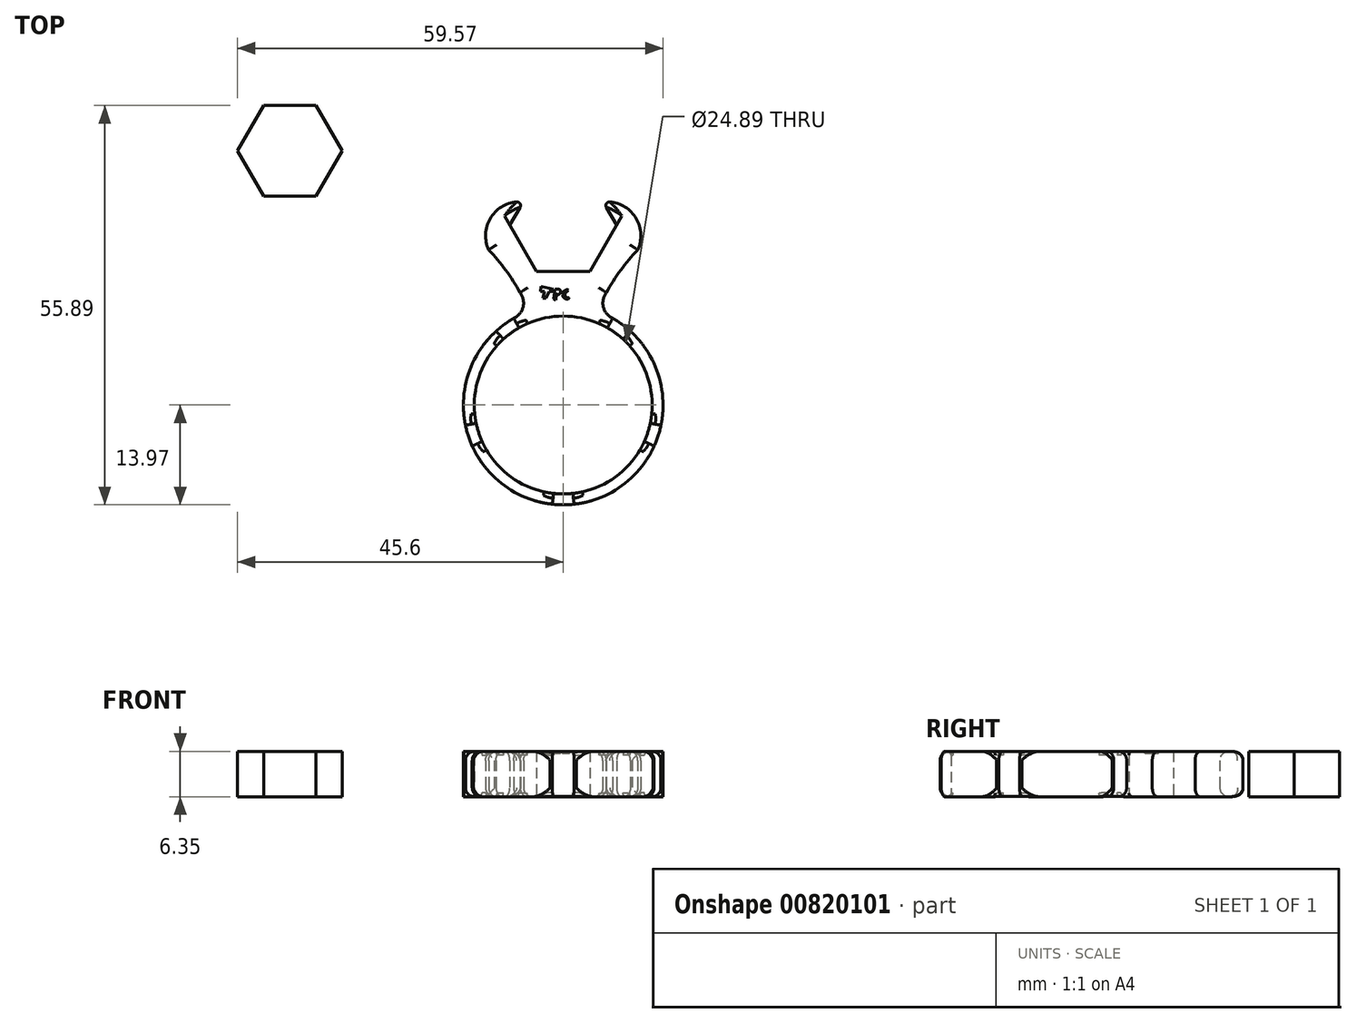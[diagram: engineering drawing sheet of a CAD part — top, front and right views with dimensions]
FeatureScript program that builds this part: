
annotation { "Feature Type Name" : "Feature", "Feature Type Description" : "" }
export const myFeature = defineFeature(function(context is Context, id is Id, definition is map)
    precondition{}
    {
        {
            var Q0;
            Q0=qCreatedBy(makeId("Top.planeOp"),FACE);
            var sketch = newSketch(context, id + "F0", { "sketchPlane" : qUnion([Q0])});
            skCircle(sketch, "E0", {"center": v(0, 0) * mm, "radius": 31.75 * mm, "construction": true});
            skCircle(sketch, "E1", {"center": v(0, 0) * mm, "radius": 12.45 * mm});
            skCircle(sketch, "E2.cCircle", {"center": v(0, 25.18) * mm, "radius": 6.48 * mm, "construction": true});
            skLineSegment(sketch, "E2.0", {"start": v(-3.74, 18.7) * mm, "end": v(-7.48, 25.18) * mm});
            skLineSegment(sketch, "E2.1", {"start": v(-7.48, 25.18) * mm, "end": v(-3.74, 31.66) * mm});
            skLineSegment(sketch, "E2.2", {"start": v(-3.74, 31.66) * mm, "end": v(3.74, 31.66) * mm});
            skLineSegment(sketch, "E2.3", {"start": v(3.74, 31.66) * mm, "end": v(7.48, 25.18) * mm});
            skLineSegment(sketch, "E2.4", {"start": v(7.48, 25.18) * mm, "end": v(3.74, 18.7) * mm});
            skLineSegment(sketch, "E2.5", {"start": v(3.74, 18.7) * mm, "end": v(-3.74, 18.7) * mm});
            skPoint(sketch, "E2.0.midPoint", {"position": v(-5.5, 18.96) * mm});
            skCircle(sketch, "E3", {"center": v(0, 0) * mm, "radius": 13.97 * mm});
            skArc(sketch, "E4", {"start": v(-5.6, 28.42) * mm, "mid": v(-9.97, 26.47) * mm, "end": v(-10.43, 21.7) * mm});
            skArc(sketch, "E5", {"start": v(-6.03, 15.72) * mm, "mid": v(-8.04, 18.85) * mm, "end": v(-10.43, 21.7) * mm});
            skArc(sketch, "E6", {"start": v(-6.92, 12.14) * mm, "mid": v(-5.62, 13.72) * mm, "end": v(-6.03, 15.72) * mm});
            skArc(sketch, "E7.MirrorCS", {"start": v(5.6, 28.42) * mm, "mid": v(9.97, 26.47) * mm, "end": v(10.43, 21.7) * mm});
            skArc(sketch, "E8.MirrorCS", {"start": v(6.03, 15.72) * mm, "mid": v(8.04, 18.85) * mm, "end": v(10.43, 21.7) * mm});
            skArc(sketch, "E9.MirrorCS", {"start": v(6.92, 12.14) * mm, "mid": v(5.62, 13.72) * mm, "end": v(6.03, 15.72) * mm});
            skArc(sketch, "E10.1.0", {"start": v(-25.3, 14.12) * mm, "mid": v(-22.09, 17.66) * mm, "end": v(-17.42, 16.63) * mm});
            skArc(sketch, "E10.1.1", {"start": v(-13.1, 10.6) * mm, "mid": v(-15.45, 13.47) * mm, "end": v(-17.42, 16.63) * mm});
            skCircle(sketch, "E10.1.2", {"center": v(-23.95, 7.78) * mm, "radius": 6.48 * mm, "construction": true});
            skLineSegment(sketch, "E10.1.3", {"start": v(-31.26, 6.23) * mm, "end": v(-28.95, 13.34) * mm});
            skLineSegment(sketch, "E10.1.4", {"start": v(-21.64, 14.9) * mm, "end": v(-16.63, 9.34) * mm});
            skArc(sketch, "E10.1.5", {"start": v(-28.76, 3.45) * mm, "mid": v(-28.25, -1.3) * mm, "end": v(-23.87, -3.21) * mm});
            skArc(sketch, "E10.1.6", {"start": v(-16.82, -0.87) * mm, "mid": v(-20.42, -1.82) * mm, "end": v(-23.87, -3.21) * mm});
            skPoint(sketch, "E10.1.7", {"position": v(-19.73, 0.63) * mm});
            skArc(sketch, "E10.1.8", {"start": v(-9.4, 10.33) * mm, "mid": v(-11.31, 9.58) * mm, "end": v(-13.1, 10.6) * mm});
            skLineSegment(sketch, "E10.1.9", {"start": v(-18.94, 2.22) * mm, "end": v(-26.26, 0.67) * mm});
            skLineSegment(sketch, "E10.1.10", {"start": v(-26.26, 0.67) * mm, "end": v(-31.26, 6.23) * mm});
            skLineSegment(sketch, "E10.1.11", {"start": v(-16.63, 9.34) * mm, "end": v(-18.94, 2.22) * mm});
            skArc(sketch, "E10.1.12", {"start": v(-13.68, -2.83) * mm, "mid": v(-14.78, -1.1) * mm, "end": v(-16.82, -0.87) * mm});
            skLineSegment(sketch, "E10.1.13", {"start": v(-28.95, 13.34) * mm, "end": v(-21.64, 14.9) * mm});
            skArc(sketch, "E10.2.0", {"start": v(-21.24, -19.7) * mm, "mid": v(-23.63, -15.55) * mm, "end": v(-21.2, -11.43) * mm});
            skArc(sketch, "E10.2.1", {"start": v(-14.12, -9.18) * mm, "mid": v(-17.59, -10.53) * mm, "end": v(-21.2, -11.43) * mm});
            skCircle(sketch, "E10.2.2", {"center": v(-14.8, -20.37) * mm, "radius": 6.48 * mm, "construction": true});
            skLineSegment(sketch, "E10.2.3", {"start": v(-15.58, -27.8) * mm, "end": v(-21.63, -23.41) * mm});
            skLineSegment(sketch, "E10.2.4", {"start": v(-20.85, -15.97) * mm, "end": v(-14.02, -12.93) * mm});
            skArc(sketch, "E10.2.5", {"start": v(-12.17, -26.29) * mm, "mid": v(-7.49, -27.27) * mm, "end": v(-4.32, -23.7) * mm});
            skArc(sketch, "E10.2.6", {"start": v(-4.37, -16.26) * mm, "mid": v(-4.58, -19.98) * mm, "end": v(-4.32, -23.7) * mm});
            skPoint(sketch, "E10.2.7", {"position": v(-6.7, -18.57) * mm});
            skArc(sketch, "E10.2.8", {"start": v(-12.73, -5.75) * mm, "mid": v(-12.6, -7.8) * mm, "end": v(-14.12, -9.18) * mm});
            skLineSegment(sketch, "E10.2.9", {"start": v(-7.97, -17.33) * mm, "end": v(-8.75, -24.77) * mm});
            skLineSegment(sketch, "E10.2.10", {"start": v(-8.75, -24.77) * mm, "end": v(-15.58, -27.8) * mm});
            skLineSegment(sketch, "E10.2.11", {"start": v(-14.02, -12.93) * mm, "end": v(-7.97, -17.33) * mm});
            skArc(sketch, "E10.2.12", {"start": v(-1.54, -13.89) * mm, "mid": v(-3.52, -14.4) * mm, "end": v(-4.37, -16.26) * mm});
            skLineSegment(sketch, "E10.2.13", {"start": v(-21.63, -23.41) * mm, "end": v(-20.85, -15.97) * mm});
            skArc(sketch, "E10.3.0", {"start": v(12.17, -26.29) * mm, "mid": v(7.49, -27.27) * mm, "end": v(4.32, -23.7) * mm});
            skArc(sketch, "E10.3.1", {"start": v(4.37, -16.26) * mm, "mid": v(4.58, -19.98) * mm, "end": v(4.32, -23.7) * mm});
            skCircle(sketch, "E10.3.2", {"center": v(14.8, -20.37) * mm, "radius": 6.48 * mm, "construction": true});
            skLineSegment(sketch, "E10.3.3", {"start": v(21.63, -23.41) * mm, "end": v(15.58, -27.8) * mm});
            skLineSegment(sketch, "E10.3.4", {"start": v(8.75, -24.77) * mm, "end": v(7.97, -17.33) * mm});
            skArc(sketch, "E10.3.5", {"start": v(21.24, -19.7) * mm, "mid": v(23.63, -15.55) * mm, "end": v(21.2, -11.43) * mm});
            skArc(sketch, "E10.3.6", {"start": v(14.12, -9.18) * mm, "mid": v(17.59, -10.53) * mm, "end": v(21.2, -11.43) * mm});
            skPoint(sketch, "E10.3.7", {"position": v(15.6, -12.1) * mm});
            skArc(sketch, "E10.3.8", {"start": v(1.54, -13.89) * mm, "mid": v(3.52, -14.4) * mm, "end": v(4.37, -16.26) * mm});
            skLineSegment(sketch, "E10.3.9", {"start": v(14.02, -12.93) * mm, "end": v(20.85, -15.97) * mm});
            skLineSegment(sketch, "E10.3.10", {"start": v(20.85, -15.97) * mm, "end": v(21.63, -23.41) * mm});
            skLineSegment(sketch, "E10.3.11", {"start": v(7.97, -17.33) * mm, "end": v(14.02, -12.93) * mm});
            skArc(sketch, "E10.3.12", {"start": v(12.73, -5.75) * mm, "mid": v(12.6, -7.8) * mm, "end": v(14.12, -9.18) * mm});
            skLineSegment(sketch, "E10.3.13", {"start": v(15.58, -27.8) * mm, "end": v(8.75, -24.77) * mm});
            skArc(sketch, "E10.4.0", {"start": v(28.76, 3.45) * mm, "mid": v(28.25, -1.3) * mm, "end": v(23.87, -3.21) * mm});
            skArc(sketch, "E10.4.1", {"start": v(16.82, -0.87) * mm, "mid": v(20.42, -1.82) * mm, "end": v(23.87, -3.21) * mm});
            skCircle(sketch, "E10.4.2", {"center": v(23.95, 7.78) * mm, "radius": 6.48 * mm, "construction": true});
            skLineSegment(sketch, "E10.4.3", {"start": v(28.95, 13.34) * mm, "end": v(31.26, 6.23) * mm});
            skLineSegment(sketch, "E10.4.4", {"start": v(26.26, 0.67) * mm, "end": v(18.94, 2.22) * mm});
            skArc(sketch, "E10.4.5", {"start": v(25.3, 14.12) * mm, "mid": v(22.09, 17.66) * mm, "end": v(17.42, 16.63) * mm});
            skArc(sketch, "E10.4.6", {"start": v(13.1, 10.6) * mm, "mid": v(15.45, 13.47) * mm, "end": v(17.42, 16.63) * mm});
            skPoint(sketch, "E10.4.7", {"position": v(16.33, 11.09) * mm});
            skArc(sketch, "E10.4.8", {"start": v(13.68, -2.83) * mm, "mid": v(14.78, -1.1) * mm, "end": v(16.82, -0.87) * mm});
            skLineSegment(sketch, "E10.4.9", {"start": v(16.63, 9.34) * mm, "end": v(21.64, 14.9) * mm});
            skLineSegment(sketch, "E10.4.10", {"start": v(21.64, 14.9) * mm, "end": v(28.95, 13.34) * mm});
            skLineSegment(sketch, "E10.4.11", {"start": v(18.94, 2.22) * mm, "end": v(16.63, 9.34) * mm});
            skArc(sketch, "E10.4.12", {"start": v(9.4, 10.33) * mm, "mid": v(11.31, 9.58) * mm, "end": v(13.1, 10.6) * mm});
            skLineSegment(sketch, "E10.4.13", {"start": v(31.26, 6.23) * mm, "end": v(26.26, 0.67) * mm});
            skSolve(sketch);
        }
        {
            var Q0;
            {var subQ0=sQuery(id+"F0.wireOp",EDGE,"08dda1b8-4bbb-4ccd-a0d6-4031cab699ba.4.4.0");var subQ1=sQuery(id+"F0.wireOp",EDGE,"E1");var subQ2=makeQuery(id+"F0.imprint","INTERSECT",VERTEX,{"derivedFrom":[subQ1,subQ0]});Q0=makeQuery(id+"F0.imprint","IMPRINT",FACE,{"disambiguationData":[TD([[makeQuery(id+"F0.imprint","IMPRINT",EDGE,{"disambiguationData":[TD([[subQ2,-1.0]])],"derivedFrom":subQ1}),-1.0]])]});}
            var Q1;
            {var subQ0=sQuery(id+"F0.wireOp",EDGE,"08dda1b8-4bbb-4ccd-a0d6-4031cab699ba.17.3.0");var subQ1=sQuery(id+"F0.wireOp",EDGE,"E1");var subQ2=makeQuery(id+"F0.imprint","INTERSECT",VERTEX,{"derivedFrom":[subQ1,subQ0]});Q1=makeQuery(id+"F0.imprint","IMPRINT",FACE,{"disambiguationData":[TD([[makeQuery(id+"F0.imprint","IMPRINT",EDGE,{"disambiguationData":[TD([[subQ2,-1.0]])],"derivedFrom":subQ1}),-1.0]])]});}
            var Q2;
            {var subQ0=sQuery(id+"F0.wireOp",EDGE,"08dda1b8-4bbb-4ccd-a0d6-4031cab699ba.4.3.0");var subQ1=sQuery(id+"F0.wireOp",EDGE,"E1");var subQ2=makeQuery(id+"F0.imprint","INTERSECT",VERTEX,{"derivedFrom":[subQ1,subQ0]});Q2=makeQuery(id+"F0.imprint","IMPRINT",FACE,{"disambiguationData":[TD([[makeQuery(id+"F0.imprint","IMPRINT",EDGE,{"disambiguationData":[TD([[subQ2,-1.0]])],"derivedFrom":subQ1}),-1.0]])]});}
            var Q3;
            {var subQ0=sQuery(id+"F0.wireOp",EDGE,"133b7ee5-6936-4400-ab5c-c1a8c481468b.2.5");var subQ1=sQuery(id+"F0.wireOp",EDGE,"E1");var subQ2=makeQuery(id+"F0.imprint","INTERSECT",VERTEX,{"derivedFrom":[subQ1,subQ0]});Q3=makeQuery(id+"F0.imprint","IMPRINT",FACE,{"disambiguationData":[TD([[makeQuery(id+"F0.imprint","IMPRINT",EDGE,{"disambiguationData":[TD([[subQ2,-1.0]])],"derivedFrom":subQ1}),-1.0]])]});}
            var Q4;
            {var subQ0=sQuery(id+"F0.wireOp",EDGE,"133b7ee5-6936-4400-ab5c-c1a8c481468b.2.1");var subQ1=sQuery(id+"F0.wireOp",EDGE,"E1");var subQ2=makeQuery(id+"F0.imprint","INTERSECT",VERTEX,{"derivedFrom":[subQ1,subQ0]});Q4=makeQuery(id+"F0.imprint","IMPRINT",FACE,{"disambiguationData":[TD([[makeQuery(id+"F0.imprint","IMPRINT",EDGE,{"disambiguationData":[TD([[subQ2,-1.0]])],"derivedFrom":subQ1}),-1.0]])]});}
            var Q5;
            {var subQ0=sQuery(id+"F0.wireOp",EDGE,"133b7ee5-6936-4400-ab5c-c1a8c481468b.1.5");var subQ1=sQuery(id+"F0.wireOp",EDGE,"E1");var subQ2=makeQuery(id+"F0.imprint","INTERSECT",VERTEX,{"derivedFrom":[subQ1,subQ0]});Q5=makeQuery(id+"F0.imprint","IMPRINT",FACE,{"disambiguationData":[TD([[makeQuery(id+"F0.imprint","IMPRINT",EDGE,{"disambiguationData":[TD([[subQ2,-1.0]])],"derivedFrom":subQ1}),-1.0]])]});}
            var Q6;
            {var subQ0=sQuery(id+"F0.wireOp",EDGE,"133b7ee5-6936-4400-ab5c-c1a8c481468b.1.1");var subQ1=sQuery(id+"F0.wireOp",EDGE,"E1");var subQ2=makeQuery(id+"F0.imprint","INTERSECT",VERTEX,{"derivedFrom":[subQ1,subQ0]});Q6=makeQuery(id+"F0.imprint","IMPRINT",FACE,{"disambiguationData":[TD([[makeQuery(id+"F0.imprint","IMPRINT",EDGE,{"disambiguationData":[TD([[subQ2,-1.0]])],"derivedFrom":subQ1}),-1.0]])]});}
            var Q7;
            {var subQ0=sQuery(id+"F0.wireOp",EDGE,"d495b0eb-ba1d-4a21-93e3-987e0228af5a");var subQ1=sQuery(id+"F0.wireOp",EDGE,"E1");var subQ2=makeQuery(id+"F0.imprint","INTERSECT",VERTEX,{"derivedFrom":[subQ1,subQ0]});Q7=makeQuery(id+"F0.imprint","IMPRINT",FACE,{"disambiguationData":[TD([[makeQuery(id+"F0.imprint","IMPRINT",EDGE,{"disambiguationData":[TD([[subQ2,-1.0]])],"derivedFrom":subQ1}),-1.0]])]});}
            var Q8;
            {var subQ0=sQuery(id+"F0.wireOp",EDGE,"d495b0eb-ba1d-4a21-93e3-987e0228af5a");var subQ1=sQuery(id+"F0.wireOp",EDGE,"E1");var subQ2=makeQuery(id+"F0.imprint","INTERSECT",VERTEX,{"derivedFrom":[subQ1,subQ0]});Q8=makeQuery(id+"F0.imprint","IMPRINT",FACE,{"disambiguationData":[TD([[makeQuery(id+"F0.imprint","IMPRINT",EDGE,{"disambiguationData":[TD([[subQ2,1.0]])],"derivedFrom":subQ1}),-1.0]])]});}
            var Q9;
            {var subQ0=sQuery(id+"F0.wireOp",EDGE,"9611d97b-251f-4bb5-bbc4-e98456876ea10.MirrorCS");var subQ1=sQuery(id+"F0.wireOp",EDGE,"E1");var subQ2=makeQuery(id+"F0.imprint","INTERSECT",VERTEX,{"derivedFrom":[subQ1,subQ0]});Q9=makeQuery(id+"F0.imprint","IMPRINT",FACE,{"disambiguationData":[TD([[makeQuery(id+"F0.imprint","IMPRINT",EDGE,{"disambiguationData":[TD([[subQ2,1.0]])],"derivedFrom":subQ1}),-1.0]])]});}
            var Q10;
            {var subQ2=sQuery(id+"F0.wireOp",EDGE,"E2.0");Q10=makeQuery(id+"F0.imprint","IMPRINT",FACE,{"disambiguationData":[TD([[makeQuery(id+"F0.imprint","IMPRINT",EDGE,{"derivedFrom":subQ2}),1.0]])]});}
            var Q11;
            Q11=makeQuery(id+"F0.imprint","IMPRINT",FACE,{"disambiguationData":[TD([[makeQuery(id+"F0.imprint","IMPRINT",EDGE,{"derivedFrom":sQuery(id+"F0.wireOp",EDGE,"08dda1b8-4bbb-4ccd-a0d6-4031cab699ba.11.4.0")}),1.0]])]});
            var Q12;
            Q12=makeQuery(id+"F0.imprint","IMPRINT",FACE,{"disambiguationData":[TD([[makeQuery(id+"F0.imprint","IMPRINT",EDGE,{"derivedFrom":sQuery(id+"F0.wireOp",EDGE,"08dda1b8-4bbb-4ccd-a0d6-4031cab699ba.11.3.0")}),1.0]])]});
            var Q13;
            {var subQ1=sQuery(id+"F0.wireOp",EDGE,"133b7ee5-6936-4400-ab5c-c1a8c481468b.2.0");Q13=makeQuery(id+"F0.imprint","IMPRINT",FACE,{"disambiguationData":[TD([[makeQuery(id+"F0.imprint","IMPRINT",EDGE,{"derivedFrom":subQ1}),1.0]])]});}
            var Q14;
            {var subQ1=sQuery(id+"F0.wireOp",EDGE,"133b7ee5-6936-4400-ab5c-c1a8c481468b.1.0");Q14=makeQuery(id+"F0.imprint","IMPRINT",FACE,{"disambiguationData":[TD([[makeQuery(id+"F0.imprint","IMPRINT",EDGE,{"derivedFrom":subQ1}),1.0]])]});}
            var Q15;
            {var subQ8=sQuery(id+"F0.wireOp",EDGE,"E10.1.0");Q15=makeQuery(id+"F0.imprint","IMPRINT",FACE,{"disambiguationData":[TD([[makeQuery(id+"F0.imprint","IMPRINT",EDGE,{"derivedFrom":subQ8}),-1.0]])]});}
            var Q16;
            {var subQ10=sQuery(id+"F0.wireOp",EDGE,"E10.2.0");Q16=makeQuery(id+"F0.imprint","IMPRINT",FACE,{"disambiguationData":[TD([[makeQuery(id+"F0.imprint","IMPRINT",EDGE,{"derivedFrom":subQ10}),-1.0]])]});}
            var Q17;
            {var subQ10=sQuery(id+"F0.wireOp",EDGE,"E10.3.0");Q17=makeQuery(id+"F0.imprint","IMPRINT",FACE,{"disambiguationData":[TD([[makeQuery(id+"F0.imprint","IMPRINT",EDGE,{"derivedFrom":subQ10}),-1.0]])]});}
            var Q18;
            {var subQ11=sQuery(id+"F0.wireOp",EDGE,"E10.4.0");Q18=makeQuery(id+"F0.imprint","IMPRINT",FACE,{"disambiguationData":[TD([[makeQuery(id+"F0.imprint","IMPRINT",EDGE,{"derivedFrom":subQ11}),-1.0]])]});}
            extrude(context, id + "F1", {"entities" : qUnion([Q0, Q1, Q2, Q3, Q4, Q5, Q6, Q7, Q8, Q9, Q10, Q11, Q12, Q13, Q14, Q15, Q16, Q17, Q18]), "depth" : 6.35 * mm, "offsetDistance" : 25.4 * mm});
        }
        {
            var Q0;
            Q0=qCreatedBy(makeId("Top.planeOp"),FACE);
            var sketch = newSketch(context, id + "F2", { "sketchPlane" : qUnion([Q0])});
            skCircle(sketch, "E11.cCircle", {"center": v(-38.26, 35.57) * mm, "radius": 6.35 * mm, "construction": true});
            skLineSegment(sketch, "E11.0", {"start": v(-34.6, 29.22) * mm, "end": v(-41.93, 29.22) * mm});
            skLineSegment(sketch, "E11.1", {"start": v(-41.93, 29.22) * mm, "end": v(-45.6, 35.57) * mm});
            skLineSegment(sketch, "E11.2", {"start": v(-45.6, 35.57) * mm, "end": v(-41.93, 41.92) * mm});
            skLineSegment(sketch, "E11.3", {"start": v(-41.93, 41.92) * mm, "end": v(-34.6, 41.92) * mm});
            skLineSegment(sketch, "E11.4", {"start": v(-34.6, 41.92) * mm, "end": v(-30.93, 35.57) * mm});
            skLineSegment(sketch, "E11.5", {"start": v(-30.93, 35.57) * mm, "end": v(-34.6, 29.22) * mm});
            skPoint(sketch, "E11.0.midPoint", {"position": v(-38.26, 29.22) * mm});
            skSolve(sketch);
        }
        {
            var Q0;
            Q0=makeQuery(id+"F2.imprint","IMPRINT",FACE,{"disambiguationData":[TD([[makeQuery(id+"F2.imprint","IMPRINT",EDGE,{"derivedFrom":sQuery(id+"F2.wireOp",EDGE,"E11.0")}),-1.0]])]});
            extrude(context, id + "F3", {"entities" : qUnion([Q0]), "depth" : 6.35 * mm, "offsetDistance" : 25.4 * mm});
        }
        {
            var Q0;
            Q0=makeQuery(id+"F1.opExtrude","SWEPT_EDGE",EDGE,{"disambiguationData":[OSD([sQuery(id+"F0.wireOp",EDGE,"E10.1.5"),sQuery(id+"F0.wireOp",EDGE,"E10.1.10")])]});
            var Q1;
            Q1=makeQuery(id+"F1.opExtrude","SWEPT_EDGE",EDGE,{"disambiguationData":[OSD([sQuery(id+"F0.wireOp",EDGE,"E10.1.0"),sQuery(id+"F0.wireOp",EDGE,"E10.1.13")])]});
            var Q2;
            Q2=makeQuery(id+"F1.opExtrude","SWEPT_EDGE",EDGE,{"disambiguationData":[OSD([sQuery(id+"F0.wireOp",EDGE,"E2.1"),sQuery(id+"F0.wireOp",EDGE,"E4")])]});
            var Q3;
            Q3=makeQuery(id+"F1.opExtrude","SWEPT_EDGE",EDGE,{"disambiguationData":[OSD([sQuery(id+"F0.wireOp",EDGE,"E2.3"),sQuery(id+"F0.wireOp",EDGE,"E7.MirrorCS")])]});
            var Q4;
            Q4=makeQuery(id+"F1.opExtrude","SWEPT_EDGE",EDGE,{"disambiguationData":[OSD([sQuery(id+"F0.wireOp",EDGE,"E10.4.0"),sQuery(id+"F0.wireOp",EDGE,"E10.4.13")])]});
            var Q5;
            Q5=makeQuery(id+"F1.opExtrude","SWEPT_EDGE",EDGE,{"disambiguationData":[OSD([sQuery(id+"F0.wireOp",EDGE,"E10.3.5"),sQuery(id+"F0.wireOp",EDGE,"E10.3.10")])]});
            var Q6;
            Q6=makeQuery(id+"F1.opExtrude","SWEPT_EDGE",EDGE,{"disambiguationData":[OSD([sQuery(id+"F0.wireOp",EDGE,"E10.3.0"),sQuery(id+"F0.wireOp",EDGE,"E10.3.13")])]});
            var Q7;
            Q7=makeQuery(id+"F1.opExtrude","SWEPT_EDGE",EDGE,{"disambiguationData":[OSD([sQuery(id+"F0.wireOp",EDGE,"E10.2.5"),sQuery(id+"F0.wireOp",EDGE,"E10.2.10")])]});
            var Q8;
            Q8=makeQuery(id+"F1.opExtrude","SWEPT_EDGE",EDGE,{"disambiguationData":[OSD([sQuery(id+"F0.wireOp",EDGE,"E10.2.0"),sQuery(id+"F0.wireOp",EDGE,"E10.2.13")])]});
            var Q9;
            Q9=makeQuery(id+"F1.opExtrude","SWEPT_EDGE",EDGE,{"disambiguationData":[OSD([sQuery(id+"F0.wireOp",EDGE,"E10.4.5"),sQuery(id+"F0.wireOp",EDGE,"E10.4.10")])]});
            fillet(context, id + "F4", {"entities" : qUnion([Q0, Q1, Q2, Q3, Q4, Q5, Q6, Q7, Q8, Q9]), "radius" : 0.5 * mm, "tangentPropagation" : true, "allowEdgeOverflow" : false});
        }
        {
            var Q0;
            Q0=makeQuery(id+"F1.opExtrude","CAP_EDGE",EDGE,{"disambiguationData":[OSD([sQuery(id+"F0.wireOp",EDGE,"E10.2.0")])],"isStart":false});
            var Q1;
            Q1=makeQuery(id+"F1.opExtrude","CAP_EDGE",EDGE,{"disambiguationData":[OSD([sQuery(id+"F0.wireOp",EDGE,"E10.2.1")])],"isStart":false});
            var Q2;
            Q2=makeQuery(id+"F1.opExtrude","CAP_EDGE",EDGE,{"disambiguationData":[OSD([sQuery(id+"F0.wireOp",EDGE,"E10.2.8")])],"isStart":false});
            var Q3;
            {var subQ0=sQuery(id+"F0.wireOp",EDGE,"E3");Q3=makeQuery(id+"F1.opExtrude","CAP_EDGE",EDGE,{"disambiguationData":[OSD([subQ0]),TDD([makeQuery(id+"F0.imprint","IMPRINT",EDGE,{"disambiguationData":[TD([[makeQuery(id+"F0.imprint","INTERSECT",VERTEX,{"disambiguationData":[OD(0.0)],"derivedFrom":[subQ0,sQuery(id+"F0.wireOp",EDGE,"E10.1.12")]}),-1.0]])],"derivedFrom":subQ0})])],"isStart":false});}
            var Q4;
            Q4=makeQuery(id+"F1.opExtrude","CAP_EDGE",EDGE,{"disambiguationData":[OSD([sQuery(id+"F0.wireOp",EDGE,"E10.1.12")])],"isStart":false});
            var Q5;
            Q5=makeQuery(id+"F1.opExtrude","CAP_EDGE",EDGE,{"disambiguationData":[OSD([sQuery(id+"F0.wireOp",EDGE,"E10.1.6")])],"isStart":false});
            var Q6;
            Q6=makeQuery(id+"F1.opExtrude","CAP_EDGE",EDGE,{"disambiguationData":[OSD([sQuery(id+"F0.wireOp",EDGE,"E10.1.5")])],"isStart":false});
            var Q7;
            Q7=makeQuery(id+"F1.opExtrude","CAP_EDGE",EDGE,{"disambiguationData":[OSD([sQuery(id+"F0.wireOp",EDGE,"E10.1.0")])],"isStart":false});
            var Q8;
            Q8=makeQuery(id+"F1.opExtrude","CAP_EDGE",EDGE,{"disambiguationData":[OSD([sQuery(id+"F0.wireOp",EDGE,"E10.1.1")])],"isStart":false});
            var Q9;
            Q9=makeQuery(id+"F1.opExtrude","CAP_EDGE",EDGE,{"disambiguationData":[OSD([sQuery(id+"F0.wireOp",EDGE,"E10.1.8")])],"isStart":false});
            var Q10;
            {var subQ0=sQuery(id+"F0.wireOp",EDGE,"E3");Q10=makeQuery(id+"F1.opExtrude","CAP_EDGE",EDGE,{"disambiguationData":[OSD([subQ0]),TDD([makeQuery(id+"F0.imprint","IMPRINT",EDGE,{"disambiguationData":[TD([[makeQuery(id+"F0.imprint","INTERSECT",VERTEX,{"disambiguationData":[OD(0.0)],"derivedFrom":[subQ0,sQuery(id+"F0.wireOp",EDGE,"E6")]}),-1.0]])],"derivedFrom":subQ0})])],"isStart":false});}
            var Q11;
            Q11=makeQuery(id+"F1.opExtrude","CAP_EDGE",EDGE,{"disambiguationData":[OSD([sQuery(id+"F0.wireOp",EDGE,"E6")])],"isStart":false});
            var Q12;
            Q12=makeQuery(id+"F1.opExtrude","CAP_EDGE",EDGE,{"disambiguationData":[OSD([sQuery(id+"F0.wireOp",EDGE,"E5")])],"isStart":false});
            var Q13;
            Q13=makeQuery(id+"F1.opExtrude","CAP_EDGE",EDGE,{"disambiguationData":[OSD([sQuery(id+"F0.wireOp",EDGE,"E4")])],"isStart":false});
            var Q14;
            Q14=makeQuery(id+"F1.opExtrude","CAP_EDGE",EDGE,{"disambiguationData":[OSD([sQuery(id+"F0.wireOp",EDGE,"E8.MirrorCS")])],"isStart":false});
            var Q15;
            Q15=makeQuery(id+"F1.opExtrude","CAP_EDGE",EDGE,{"disambiguationData":[OSD([sQuery(id+"F0.wireOp",EDGE,"E7.MirrorCS")])],"isStart":false});
            var Q16;
            Q16=makeQuery(id+"F1.opExtrude","CAP_EDGE",EDGE,{"disambiguationData":[OSD([sQuery(id+"F0.wireOp",EDGE,"E9.MirrorCS")])],"isStart":false});
            var Q17;
            Q17=makeQuery(id+"F1.opExtrude","CAP_EDGE",EDGE,{"disambiguationData":[OSD([sQuery(id+"F0.wireOp",EDGE,"E9.MirrorCS")])],"isStart":true});
            var Q18;
            Q18=makeQuery(id+"F1.opExtrude","CAP_EDGE",EDGE,{"disambiguationData":[OSD([sQuery(id+"F0.wireOp",EDGE,"E10.4.12")])],"isStart":false});
            var Q19;
            {var subQ0=sQuery(id+"F0.wireOp",EDGE,"E3");Q19=makeQuery(id+"F1.opExtrude","CAP_EDGE",EDGE,{"disambiguationData":[OSD([subQ0]),TDD([makeQuery(id+"F0.imprint","IMPRINT",EDGE,{"disambiguationData":[TD([[makeQuery(id+"F0.imprint","INTERSECT",VERTEX,{"disambiguationData":[OD(0.0)],"derivedFrom":[subQ0,sQuery(id+"F0.wireOp",EDGE,"E9.MirrorCS")]}),1.0]])],"derivedFrom":subQ0})])],"isStart":false});}
            var Q20;
            {var subQ0=sQuery(id+"F0.wireOp",EDGE,"E3");Q20=makeQuery(id+"F1.opExtrude","CAP_EDGE",EDGE,{"disambiguationData":[OSD([subQ0]),TDD([makeQuery(id+"F0.imprint","IMPRINT",EDGE,{"disambiguationData":[TD([[makeQuery(id+"F0.imprint","INTERSECT",VERTEX,{"disambiguationData":[OD(0.0)],"derivedFrom":[subQ0,sQuery(id+"F0.wireOp",EDGE,"E9.MirrorCS")]}),1.0]])],"derivedFrom":subQ0})])],"isStart":true});}
            var Q21;
            Q21=makeQuery(id+"F1.opExtrude","CAP_EDGE",EDGE,{"disambiguationData":[OSD([sQuery(id+"F0.wireOp",EDGE,"E8.MirrorCS")])],"isStart":true});
            var Q22;
            Q22=makeQuery(id+"F1.opExtrude","CAP_EDGE",EDGE,{"disambiguationData":[OSD([sQuery(id+"F0.wireOp",EDGE,"E7.MirrorCS")])],"isStart":true});
            var Q23;
            Q23=makeQuery(id+"F1.opExtrude","CAP_EDGE",EDGE,{"disambiguationData":[OSD([sQuery(id+"F0.wireOp",EDGE,"E10.4.6")])],"isStart":false});
            var Q24;
            Q24=makeQuery(id+"F1.opExtrude","CAP_EDGE",EDGE,{"disambiguationData":[OSD([sQuery(id+"F0.wireOp",EDGE,"E10.4.5")])],"isStart":false});
            var Q25;
            Q25=makeQuery(id+"F1.opExtrude","CAP_EDGE",EDGE,{"disambiguationData":[OSD([sQuery(id+"F0.wireOp",EDGE,"E10.4.5")])],"isStart":true});
            var Q26;
            Q26=makeQuery(id+"F1.opExtrude","CAP_EDGE",EDGE,{"disambiguationData":[OSD([sQuery(id+"F0.wireOp",EDGE,"E10.2.5")])],"isStart":false});
            var Q27;
            Q27=makeQuery(id+"F1.opExtrude","CAP_EDGE",EDGE,{"disambiguationData":[OSD([sQuery(id+"F0.wireOp",EDGE,"E10.2.12")])],"isStart":false});
            var Q28;
            Q28=makeQuery(id+"F1.opExtrude","CAP_EDGE",EDGE,{"disambiguationData":[OSD([sQuery(id+"F0.wireOp",EDGE,"E10.2.6")])],"isStart":false});
            var Q29;
            {var subQ0=sQuery(id+"F0.wireOp",EDGE,"E3");Q29=makeQuery(id+"F1.opExtrude","CAP_EDGE",EDGE,{"disambiguationData":[OSD([subQ0]),TDD([makeQuery(id+"F0.imprint","IMPRINT",EDGE,{"disambiguationData":[TD([[makeQuery(id+"F0.imprint","INTERSECT",VERTEX,{"disambiguationData":[OD(0.0)],"derivedFrom":[subQ0,sQuery(id+"F0.wireOp",EDGE,"E10.2.12")]}),-1.0]])],"derivedFrom":subQ0})])],"isStart":false});}
            var Q30;
            Q30=makeQuery(id+"F1.opExtrude","CAP_EDGE",EDGE,{"disambiguationData":[OSD([sQuery(id+"F0.wireOp",EDGE,"E10.3.8")])],"isStart":false});
            var Q31;
            Q31=makeQuery(id+"F1.opExtrude","CAP_EDGE",EDGE,{"disambiguationData":[OSD([sQuery(id+"F0.wireOp",EDGE,"E10.3.1")])],"isStart":false});
            var Q32;
            Q32=makeQuery(id+"F1.opExtrude","CAP_EDGE",EDGE,{"disambiguationData":[OSD([sQuery(id+"F0.wireOp",EDGE,"E10.3.0")])],"isStart":false});
            var Q33;
            Q33=makeQuery(id+"F1.opExtrude","CAP_EDGE",EDGE,{"disambiguationData":[OSD([sQuery(id+"F0.wireOp",EDGE,"E10.3.5")])],"isStart":false});
            var Q34;
            Q34=makeQuery(id+"F1.opExtrude","CAP_EDGE",EDGE,{"disambiguationData":[OSD([sQuery(id+"F0.wireOp",EDGE,"E10.3.6")])],"isStart":false});
            var Q35;
            Q35=makeQuery(id+"F1.opExtrude","CAP_EDGE",EDGE,{"disambiguationData":[OSD([sQuery(id+"F0.wireOp",EDGE,"E10.3.12")])],"isStart":false});
            var Q36;
            {var subQ0=sQuery(id+"F0.wireOp",EDGE,"E3");Q36=makeQuery(id+"F1.opExtrude","CAP_EDGE",EDGE,{"disambiguationData":[OSD([subQ0]),TDD([makeQuery(id+"F0.imprint","IMPRINT",EDGE,{"disambiguationData":[TD([[makeQuery(id+"F0.imprint","INTERSECT",VERTEX,{"disambiguationData":[OD(0.0)],"derivedFrom":[subQ0,sQuery(id+"F0.wireOp",EDGE,"E10.3.12")]}),-1.0]])],"derivedFrom":subQ0})])],"isStart":false});}
            var Q37;
            Q37=makeQuery(id+"F1.opExtrude","CAP_EDGE",EDGE,{"disambiguationData":[OSD([sQuery(id+"F0.wireOp",EDGE,"E10.4.1")])],"isStart":false});
            var Q38;
            Q38=makeQuery(id+"F1.opExtrude","CAP_EDGE",EDGE,{"disambiguationData":[OSD([sQuery(id+"F0.wireOp",EDGE,"E10.4.0")])],"isStart":false});
            var Q39;
            Q39=makeQuery(id+"F1.opExtrude","CAP_EDGE",EDGE,{"disambiguationData":[OSD([sQuery(id+"F0.wireOp",EDGE,"E10.4.8")])],"isStart":false});
            var Q40;
            Q40=makeQuery(id+"F1.opExtrude","CAP_EDGE",EDGE,{"disambiguationData":[OSD([sQuery(id+"F0.wireOp",EDGE,"E10.4.6")])],"isStart":true});
            var Q41;
            Q41=makeQuery(id+"F1.opExtrude","CAP_EDGE",EDGE,{"disambiguationData":[OSD([sQuery(id+"F0.wireOp",EDGE,"E10.4.12")])],"isStart":true});
            var Q42;
            Q42=makeQuery(id+"F1.opExtrude","CAP_EDGE",EDGE,{"disambiguationData":[OSD([sQuery(id+"F0.wireOp",EDGE,"E10.4.0")])],"isStart":true});
            var Q43;
            Q43=makeQuery(id+"F1.opExtrude","CAP_EDGE",EDGE,{"disambiguationData":[OSD([sQuery(id+"F0.wireOp",EDGE,"E10.4.8")])],"isStart":true});
            var Q44;
            {var subQ0=sQuery(id+"F0.wireOp",EDGE,"E3");Q44=makeQuery(id+"F1.opExtrude","CAP_EDGE",EDGE,{"disambiguationData":[OSD([subQ0]),TDD([makeQuery(id+"F0.imprint","IMPRINT",EDGE,{"disambiguationData":[TD([[makeQuery(id+"F0.imprint","INTERSECT",VERTEX,{"disambiguationData":[OD(0.0)],"derivedFrom":[subQ0,sQuery(id+"F0.wireOp",EDGE,"E10.3.12")]}),-1.0]])],"derivedFrom":subQ0})])],"isStart":true});}
            var Q45;
            Q45=makeQuery(id+"F1.opExtrude","CAP_EDGE",EDGE,{"disambiguationData":[OSD([sQuery(id+"F0.wireOp",EDGE,"E10.4.1")])],"isStart":true});
            var Q46;
            Q46=makeQuery(id+"F1.opExtrude","CAP_EDGE",EDGE,{"disambiguationData":[OSD([sQuery(id+"F0.wireOp",EDGE,"E10.3.12")])],"isStart":true});
            var Q47;
            Q47=makeQuery(id+"F1.opExtrude","CAP_EDGE",EDGE,{"disambiguationData":[OSD([sQuery(id+"F0.wireOp",EDGE,"E10.3.6")])],"isStart":true});
            var Q48;
            Q48=makeQuery(id+"F1.opExtrude","CAP_EDGE",EDGE,{"disambiguationData":[OSD([sQuery(id+"F0.wireOp",EDGE,"E10.3.0")])],"isStart":true});
            var Q49;
            Q49=makeQuery(id+"F1.opExtrude","CAP_EDGE",EDGE,{"disambiguationData":[OSD([sQuery(id+"F0.wireOp",EDGE,"E10.3.1")])],"isStart":true});
            var Q50;
            Q50=makeQuery(id+"F1.opExtrude","CAP_EDGE",EDGE,{"disambiguationData":[OSD([sQuery(id+"F0.wireOp",EDGE,"E10.3.8")])],"isStart":true});
            var Q51;
            Q51=makeQuery(id+"F1.opExtrude","CAP_EDGE",EDGE,{"disambiguationData":[OSD([sQuery(id+"F0.wireOp",EDGE,"E10.3.5")])],"isStart":true});
            var Q52;
            {var subQ0=sQuery(id+"F0.wireOp",EDGE,"E3");Q52=makeQuery(id+"F1.opExtrude","CAP_EDGE",EDGE,{"disambiguationData":[OSD([subQ0]),TDD([makeQuery(id+"F0.imprint","IMPRINT",EDGE,{"disambiguationData":[TD([[makeQuery(id+"F0.imprint","INTERSECT",VERTEX,{"disambiguationData":[OD(0.0)],"derivedFrom":[subQ0,sQuery(id+"F0.wireOp",EDGE,"E10.2.12")]}),-1.0]])],"derivedFrom":subQ0})])],"isStart":true});}
            var Q53;
            Q53=makeQuery(id+"F1.opExtrude","CAP_EDGE",EDGE,{"disambiguationData":[OSD([sQuery(id+"F0.wireOp",EDGE,"E10.2.12")])],"isStart":true});
            var Q54;
            Q54=makeQuery(id+"F1.opExtrude","CAP_EDGE",EDGE,{"disambiguationData":[OSD([sQuery(id+"F0.wireOp",EDGE,"E10.2.6")])],"isStart":true});
            var Q55;
            {var subQ0=sQuery(id+"F0.wireOp",EDGE,"E3");Q55=makeQuery(id+"F1.opExtrude","CAP_EDGE",EDGE,{"disambiguationData":[OSD([subQ0]),TDD([makeQuery(id+"F0.imprint","IMPRINT",EDGE,{"disambiguationData":[TD([[makeQuery(id+"F0.imprint","INTERSECT",VERTEX,{"disambiguationData":[OD(0.0)],"derivedFrom":[subQ0,sQuery(id+"F0.wireOp",EDGE,"E10.1.12")]}),-1.0]])],"derivedFrom":subQ0})])],"isStart":true});}
            var Q56;
            Q56=makeQuery(id+"F1.opExtrude","CAP_EDGE",EDGE,{"disambiguationData":[OSD([sQuery(id+"F0.wireOp",EDGE,"E4")])],"isStart":true});
            var Q57;
            Q57=makeQuery(id+"F1.opExtrude","CAP_EDGE",EDGE,{"disambiguationData":[OSD([sQuery(id+"F0.wireOp",EDGE,"E10.1.0")])],"isStart":true});
            var Q58;
            Q58=makeQuery(id+"F1.opExtrude","CAP_EDGE",EDGE,{"disambiguationData":[OSD([sQuery(id+"F0.wireOp",EDGE,"E10.1.1")])],"isStart":true});
            var Q59;
            Q59=makeQuery(id+"F1.opExtrude","CAP_EDGE",EDGE,{"disambiguationData":[OSD([sQuery(id+"F0.wireOp",EDGE,"E5")])],"isStart":true});
            var Q60;
            Q60=makeQuery(id+"F1.opExtrude","CAP_EDGE",EDGE,{"disambiguationData":[OSD([sQuery(id+"F0.wireOp",EDGE,"E6")])],"isStart":true});
            var Q61;
            Q61=makeQuery(id+"F1.opExtrude","CAP_EDGE",EDGE,{"disambiguationData":[OSD([sQuery(id+"F0.wireOp",EDGE,"E10.1.12")])],"isStart":true});
            var Q62;
            Q62=makeQuery(id+"F1.opExtrude","CAP_EDGE",EDGE,{"disambiguationData":[OSD([sQuery(id+"F0.wireOp",EDGE,"E10.1.6")])],"isStart":true});
            var Q63;
            Q63=makeQuery(id+"F1.opExtrude","CAP_EDGE",EDGE,{"disambiguationData":[OSD([sQuery(id+"F0.wireOp",EDGE,"E10.1.5")])],"isStart":true});
            var Q64;
            Q64=makeQuery(id+"F1.opExtrude","CAP_EDGE",EDGE,{"disambiguationData":[OSD([sQuery(id+"F0.wireOp",EDGE,"E10.2.1")])],"isStart":true});
            var Q65;
            Q65=makeQuery(id+"F1.opExtrude","CAP_EDGE",EDGE,{"disambiguationData":[OSD([sQuery(id+"F0.wireOp",EDGE,"E10.2.8")])],"isStart":true});
            var Q66;
            Q66=makeQuery(id+"F1.opExtrude","CAP_EDGE",EDGE,{"disambiguationData":[OSD([sQuery(id+"F0.wireOp",EDGE,"E10.2.0")])],"isStart":true});
            var Q67;
            Q67=makeQuery(id+"F1.opExtrude","CAP_EDGE",EDGE,{"disambiguationData":[OSD([sQuery(id+"F0.wireOp",EDGE,"E10.2.5")])],"isStart":true});
            var Q68;
            Q68=makeQuery(id+"F1.opExtrude","CAP_EDGE",EDGE,{"disambiguationData":[OSD([sQuery(id+"F0.wireOp",EDGE,"E10.1.8")])],"isStart":true});
            var Q69;
            {var subQ0=sQuery(id+"F0.wireOp",EDGE,"E3");Q69=makeQuery(id+"F1.opExtrude","CAP_EDGE",EDGE,{"disambiguationData":[OSD([subQ0]),TDD([makeQuery(id+"F0.imprint","IMPRINT",EDGE,{"disambiguationData":[TD([[makeQuery(id+"F0.imprint","INTERSECT",VERTEX,{"disambiguationData":[OD(0.0)],"derivedFrom":[subQ0,sQuery(id+"F0.wireOp",EDGE,"E6")]}),-1.0]])],"derivedFrom":subQ0})])],"isStart":true});}
            fillet(context, id + "F5", {"entities" : qUnion([Q0, Q1, Q2, Q3, Q4, Q5, Q6, Q7, Q8, Q9, Q10, Q11, Q12, Q13, Q14, Q15, Q16, Q17, Q18, Q19, Q20, Q21, Q22, Q23, Q24, Q25, Q26, Q27, Q28, Q29, Q30, Q31, Q32, Q33, Q34, Q35, Q36, Q37, Q38, Q39, Q40, Q41, Q42, Q43, Q44, Q45, Q46, Q47, Q48, Q49, Q50, Q51, Q52, Q53, Q54, Q55, Q56, Q57, Q58, Q59, Q60, Q61, Q62, Q63, Q64, Q65, Q66, Q67, Q68, Q69]), "radius" : 1.27 * mm, "tangentPropagation" : true, "allowEdgeOverflow" : false});
        }
        {
            var Q0;
            Q0=makeQuery(id+"F1.opExtrude","CAP_EDGE",EDGE,{"disambiguationData":[OSD([sQuery(id+"F0.wireOp",EDGE,"E1")])],"isStart":true});
            var Q1;
            Q1=makeQuery(id+"F1.opExtrude","CAP_EDGE",EDGE,{"disambiguationData":[OSD([sQuery(id+"F0.wireOp",EDGE,"E1")])],"isStart":false});
            fillet(context, id + "F6", {"entities" : qUnion([Q0, Q1]), "radius" : 0.5 * mm, "tangentPropagation" : true, "allowEdgeOverflow" : false});
        }
        {
            var Q0;
            Q0=makeQuery(id+"F6.opFillet","SPLIT",FACE,{"disambiguationData":[OD(0.0)],"derivedFrom":makeQuery(id+"F1.opExtrude","CAP_FACE",FACE,{"disambiguationData":[OSD([sQuery(id+"F0.wireOp",EDGE,"E1"),sQuery(id+"F0.wireOp",EDGE,"E2.0"),sQuery(id+"F0.wireOp",EDGE,"E2.1"),sQuery(id+"F0.wireOp",EDGE,"E2.3"),sQuery(id+"F0.wireOp",EDGE,"E2.4"),sQuery(id+"F0.wireOp",EDGE,"E2.5"),sQuery(id+"F0.wireOp",EDGE,"E3"),sQuery(id+"F0.wireOp",EDGE,"E4"),sQuery(id+"F0.wireOp",EDGE,"E5"),sQuery(id+"F0.wireOp",EDGE,"E6"),sQuery(id+"F0.wireOp",EDGE,"E7.MirrorCS"),sQuery(id+"F0.wireOp",EDGE,"E8.MirrorCS"),sQuery(id+"F0.wireOp",EDGE,"E9.MirrorCS"),sQuery(id+"F0.wireOp",EDGE,"E10.1.0"),sQuery(id+"F0.wireOp",EDGE,"E10.1.1"),sQuery(id+"F0.wireOp",EDGE,"E10.1.4"),sQuery(id+"F0.wireOp",EDGE,"E10.1.5"),sQuery(id+"F0.wireOp",EDGE,"E10.1.6"),sQuery(id+"F0.wireOp",EDGE,"E10.1.8"),sQuery(id+"F0.wireOp",EDGE,"E10.1.9"),sQuery(id+"F0.wireOp",EDGE,"E10.1.10"),sQuery(id+"F0.wireOp",EDGE,"E10.1.11"),sQuery(id+"F0.wireOp",EDGE,"E10.1.12"),sQuery(id+"F0.wireOp",EDGE,"E10.1.13"),sQuery(id+"F0.wireOp",EDGE,"E10.2.0"),sQuery(id+"F0.wireOp",EDGE,"E10.2.1"),sQuery(id+"F0.wireOp",EDGE,"E10.2.4"),sQuery(id+"F0.wireOp",EDGE,"E10.2.5"),sQuery(id+"F0.wireOp",EDGE,"E10.2.6"),sQuery(id+"F0.wireOp",EDGE,"E10.2.8"),sQuery(id+"F0.wireOp",EDGE,"E10.2.9"),sQuery(id+"F0.wireOp",EDGE,"E10.2.10"),sQuery(id+"F0.wireOp",EDGE,"E10.2.11"),sQuery(id+"F0.wireOp",EDGE,"E10.2.12"),sQuery(id+"F0.wireOp",EDGE,"E10.2.13"),sQuery(id+"F0.wireOp",EDGE,"E10.3.0"),sQuery(id+"F0.wireOp",EDGE,"E10.3.1"),sQuery(id+"F0.wireOp",EDGE,"E10.3.4"),sQuery(id+"F0.wireOp",EDGE,"E10.3.5"),sQuery(id+"F0.wireOp",EDGE,"E10.3.6"),sQuery(id+"F0.wireOp",EDGE,"E10.3.8"),sQuery(id+"F0.wireOp",EDGE,"E10.3.9"),sQuery(id+"F0.wireOp",EDGE,"E10.3.10"),sQuery(id+"F0.wireOp",EDGE,"E10.3.11"),sQuery(id+"F0.wireOp",EDGE,"E10.3.12"),sQuery(id+"F0.wireOp",EDGE,"E10.3.13"),sQuery(id+"F0.wireOp",EDGE,"E10.4.0"),sQuery(id+"F0.wireOp",EDGE,"E10.4.1"),sQuery(id+"F0.wireOp",EDGE,"E10.4.4"),sQuery(id+"F0.wireOp",EDGE,"E10.4.5"),sQuery(id+"F0.wireOp",EDGE,"E10.4.6"),sQuery(id+"F0.wireOp",EDGE,"E10.4.8"),sQuery(id+"F0.wireOp",EDGE,"E10.4.9"),sQuery(id+"F0.wireOp",EDGE,"E10.4.10"),sQuery(id+"F0.wireOp",EDGE,"E10.4.11"),sQuery(id+"F0.wireOp",EDGE,"E10.4.12"),sQuery(id+"F0.wireOp",EDGE,"E10.4.13")])],"isStart":false})});
            var sketch = newSketch(context, id + "F7", { "sketchPlane" : qUnion([Q0])});
            skLineSegment(sketch, "E12", {"start": v(-3.12, 16.6) * mm, "end": v(-1.43, 16.23) * mm});
            skLineSegment(sketch, "E13", {"start": v(-1.43, 16.23) * mm, "end": v(-1.43, 15.92) * mm});
            skLineSegment(sketch, "E14", {"start": v(-1.43, 15.92) * mm, "end": v(-3.17, 15.92) * mm});
            skLineSegment(sketch, "E15", {"start": v(-3.17, 15.92) * mm, "end": v(-3.12, 16.6) * mm});
            skLineSegment(sketch, "E16", {"start": v(-2.63, 15.92) * mm, "end": v(-2.88, 14.95) * mm});
            skLineSegment(sketch, "E17", {"start": v(-2.88, 14.95) * mm, "end": v(-2.4, 14.95) * mm});
            skLineSegment(sketch, "E18", {"start": v(-2.4, 14.95) * mm, "end": v(-2, 15.92) * mm});
            skLineSegment(sketch, "E19", {"start": v(-2, 15.92) * mm, "end": v(-2.63, 15.92) * mm});
            skLineSegment(sketch, "E20", {"start": v(-1.16, 16.24) * mm, "end": v(-1.33, 14.9) * mm});
            skLineSegment(sketch, "E21", {"start": v(-1.33, 14.9) * mm, "end": v(-1.03, 14.68) * mm});
            skLineSegment(sketch, "E22", {"start": v(-1.03, 14.68) * mm, "end": v(-0.93, 15.52) * mm});
            skArc(sketch, "E23", {"start": v(-0.93, 15.52) * mm, "mid": v(-0.36, 15.8) * mm, "end": v(-0.83, 16.23) * mm});
            skLineSegment(sketch, "E24", {"start": v(-0.83, 16.23) * mm, "end": v(-1.16, 16.24) * mm});
            skArc(sketch, "E25", {"start": v(0.72, 16.1) * mm, "mid": v(-0.1, 15.47) * mm, "end": v(0.71, 14.82) * mm});
            skLineSegment(sketch, "E26", {"start": v(0.72, 16.1) * mm, "end": v(0.57, 15.87) * mm});
            skLineSegment(sketch, "E27", {"start": v(0.71, 14.82) * mm, "end": v(0.89, 15.04) * mm});
            skArc(sketch, "E28", {"start": v(0.57, 15.87) * mm, "mid": v(0.29, 15.3) * mm, "end": v(0.89, 15.04) * mm});
            skSolve(sketch);
        }
        {
            var Q0;
            Q0=makeQuery(id+"F7.imprint","IMPRINT",FACE,{"disambiguationData":[TD([[makeQuery(id+"F7.imprint","IMPRINT",EDGE,{"derivedFrom":sQuery(id+"F7.wireOp",EDGE,"E16")}),1.0]])]});
            var Q1;
            Q1=makeQuery(id+"F7.imprint","IMPRINT",FACE,{"disambiguationData":[TD([[makeQuery(id+"F7.imprint","IMPRINT",EDGE,{"derivedFrom":sQuery(id+"F7.wireOp",EDGE,"E12")}),-1.0]])]});
            var Q2;
            Q2=makeQuery(id+"F7.imprint","IMPRINT",FACE,{"disambiguationData":[TD([[makeQuery(id+"F7.imprint","IMPRINT",EDGE,{"derivedFrom":sQuery(id+"F7.wireOp",EDGE,"E20")}),1.0]])]});
            var Q3;
            Q3=makeQuery(id+"F7.imprint","IMPRINT",FACE,{"disambiguationData":[TD([[makeQuery(id+"F7.imprint","IMPRINT",EDGE,{"derivedFrom":sQuery(id+"F7.wireOp",EDGE,"E25")}),1.0]])]});
            extrude(context, id + "F8", {"entities" : qUnion([Q0, Q1, Q2, Q3]), "operationType" : NewBodyOperationType.REMOVE, "oppositeDirection" : true, "depth" : 0.25 * mm, "offsetDistance" : 25.4 * mm});
        }
    });
